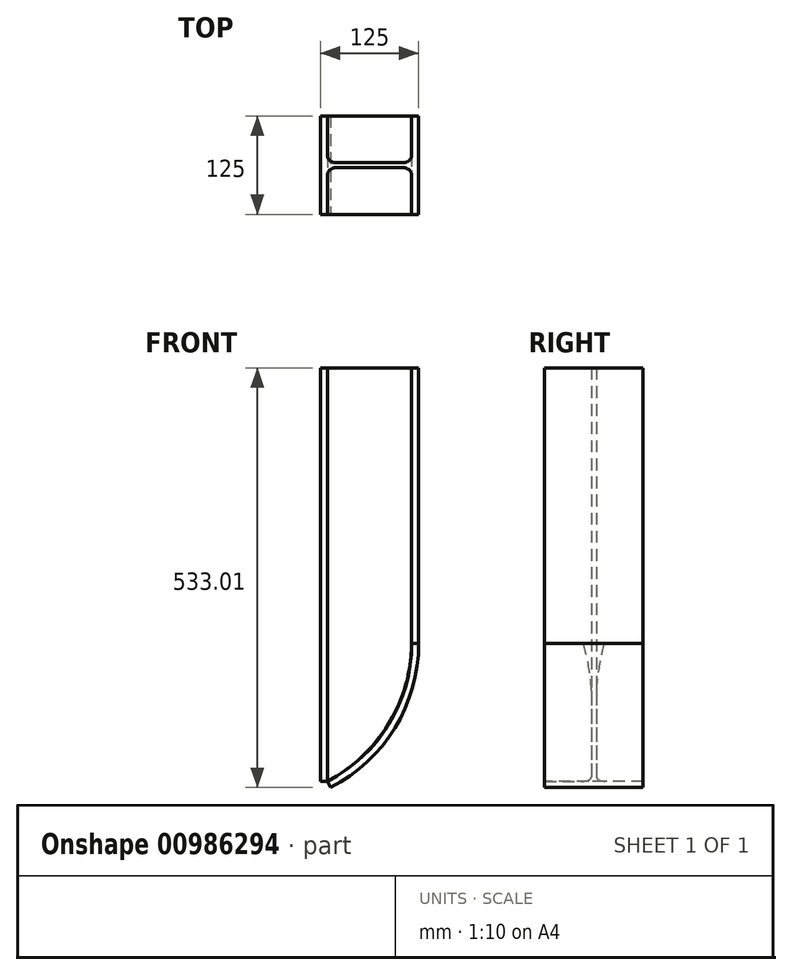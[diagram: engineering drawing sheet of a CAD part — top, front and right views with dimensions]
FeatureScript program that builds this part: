
annotation { "Feature Type Name" : "Feature", "Feature Type Description" : "" }
export const myFeature = defineFeature(function(context is Context, id is Id, definition is map)
    precondition{}
    {
        {
            var Q0;
            Q0=qCreatedBy(makeId("Top.planeOp"),FACE);
            var sketch = newSketch(context, id + "F0", { "sketchPlane" : qUnion([Q0])});
            skLineSegment(sketch, "E0.bottom", {"start": v(-62.5, 62.5) * mm, "end": v(62.5, 62.5) * mm});
            skLineSegment(sketch, "E0.top", {"start": v(-62.5, -62.5) * mm, "end": v(62.5, -62.5) * mm});
            skLineSegment(sketch, "E0.left", {"start": v(-62.5, 62.5) * mm, "end": v(-62.5, -62.5) * mm});
            skLineSegment(sketch, "E0.right", {"start": v(62.5, 62.5) * mm, "end": v(62.5, -62.5) * mm});
            skLineSegment(sketch, "E1.bottom", {"start": v(-53.5, 62.5) * mm, "end": v(53.5, 62.5) * mm});
            skLineSegment(sketch, "E1.top", {"start": v(-43.5, 3.25) * mm, "end": v(43.5, 3.25) * mm});
            skLineSegment(sketch, "E1.left", {"start": v(-53.5, 62.5) * mm, "end": v(-53.5, 13.25) * mm});
            skLineSegment(sketch, "E1.right", {"start": v(53.5, 62.5) * mm, "end": v(53.5, 13.25) * mm});
            skLineSegment(sketch, "E2.bottom", {"start": v(-53.5, -62.5) * mm, "end": v(53.5, -62.5) * mm});
            skLineSegment(sketch, "E2.top", {"start": v(-43.5, -3.25) * mm, "end": v(43.5, -3.25) * mm});
            skLineSegment(sketch, "E2.left", {"start": v(-53.5, -62.5) * mm, "end": v(-53.5, -13.25) * mm});
            skLineSegment(sketch, "E2.right", {"start": v(53.5, -62.5) * mm, "end": v(53.5, -13.25) * mm});
            skPoint(sketch, "E3.visualSharp", {"position": v(-53.5, 3.25) * mm});
            skArc(sketch, "E3.filletArc", {"start": v(-53.5, 13.25) * mm, "mid": v(-50.57, 6.18) * mm, "end": v(-43.5, 3.25) * mm});
            skPoint(sketch, "E4.visualSharp", {"position": v(53.5, 3.25) * mm});
            skArc(sketch, "E4.filletArc", {"start": v(43.5, 3.25) * mm, "mid": v(50.57, 6.18) * mm, "end": v(53.5, 13.25) * mm});
            skPoint(sketch, "E5.visualSharp", {"position": v(-53.5, -3.25) * mm});
            skArc(sketch, "E5.filletArc", {"start": v(-43.5, -3.25) * mm, "mid": v(-50.57, -6.18) * mm, "end": v(-53.5, -13.25) * mm});
            skPoint(sketch, "E6.visualSharp", {"position": v(53.5, -3.25) * mm});
            skArc(sketch, "E6.filletArc", {"start": v(53.5, -13.25) * mm, "mid": v(50.57, -6.18) * mm, "end": v(43.5, -3.25) * mm});
            skSolve(sketch);
        }
        {
            var Q0;
            {var subQ3=sQuery(id+"F0.wireOp",EDGE,"E0.left");Q0=makeQuery(id+"F0.imprint","IMPRINT",FACE,{"disambiguationData":[TD([[makeQuery(id+"F0.imprint","IMPRINT",EDGE,{"derivedFrom":subQ3}),1.0]])]});}
            extrude(context, id + "F1", {"entities" : qUnion([Q0]), "depth" : 525 * mm, "offsetDistance" : 25 * mm});
        }
        {
            var Q0;
            {var subQ0=sQuery(id+"F0.wireOp",EDGE,"E0.top");Q0=makeQuery(id+"F1.opExtrude","SWEPT_FACE",FACE,{"disambiguationData":[OSD([subQ0]),TDD([makeQuery(id+"F0.imprint","IMPRINT",EDGE,{"disambiguationData":[TD([[makeQuery(id+"F0.imprint","INTERSECT",VERTEX,{"derivedFrom":[subQ0,sQuery(id+"F0.wireOp",EDGE,"E0.left")]}),-1.0]])],"derivedFrom":subQ0})])]});}
            var sketch = newSketch(context, id + "F2", { "sketchPlane" : qUnion([Q0])});
            skLineSegment(sketch, "E7.bottom", {"start": v(-53.5, 0) * mm, "end": v(62.5, 0) * mm});
            skLineSegment(sketch, "E7.top", {"start": v(-53.5, 175) * mm, "end": v(62.5, 175) * mm});
            skLineSegment(sketch, "E7.left", {"start": v(-53.5, 0) * mm, "end": v(-53.5, 175) * mm});
            skLineSegment(sketch, "E7.right", {"start": v(62.5, 0) * mm, "end": v(62.5, 175) * mm});
            skArc(sketch, "E8", {"start": v(-53.5, 0) * mm, "mid": v(24.14, 72.74) * mm, "end": v(53.5, 175) * mm});
            skSolve(sketch);
        }
        {
            var Q0;
            Q0=makeQuery(id+"F2.imprint","IMPRINT",FACE,{"disambiguationData":[TD([[makeQuery(id+"F2.imprint","IMPRINT",EDGE,{"derivedFrom":sQuery(id+"F2.wireOp",EDGE,"E7.bottom")}),1.0]])]});
            extrude(context, id + "F3", {"entities" : qUnion([Q0]), "operationType" : NewBodyOperationType.REMOVE, "oppositeDirection" : true, "depth" : 125 * mm, "offsetDistance" : 25 * mm});
        }
        {
            var Q0;
            {var subQ0=sQuery(id+"F0.wireOp",EDGE,"E0.top");Q0=makeQuery(id+"F1.opExtrude","SWEPT_FACE",FACE,{"disambiguationData":[OSD([subQ0]),TDD([makeQuery(id+"F0.imprint","IMPRINT",EDGE,{"disambiguationData":[TD([[makeQuery(id+"F0.imprint","INTERSECT",VERTEX,{"derivedFrom":[subQ0,sQuery(id+"F0.wireOp",EDGE,"E0.right")]}),1.0]])],"derivedFrom":subQ0})])]});}
            var sketch = newSketch(context, id + "F4", { "sketchPlane" : qUnion([Q0])});
            skArc(sketch, "E9", {"start": v(-53.45, 0) * mm, "mid": v(24.65, 72.45) * mm, "end": v(53.5, 175) * mm});
            skArc(sketch, "E10.0", {"start": v(-49.34, -8) * mm, "mid": v(32.33, 67.76) * mm, "end": v(62.5, 175) * mm});
            skLineSegment(sketch, "E11", {"start": v(53.5, 175) * mm, "end": v(62.5, 175) * mm});
            skLineSegment(sketch, "E12", {"start": v(-53.45, 0) * mm, "end": v(-49.34, -8) * mm});
            skSolve(sketch);
        }
        {
            var Q0;
            Q0=makeQuery(id+"F4.imprint","IMPRINT",FACE,{"disambiguationData":[TD([[makeQuery(id+"F4.imprint","IMPRINT",EDGE,{"derivedFrom":sQuery(id+"F4.wireOp",EDGE,"E9")}),-1.0]])]});
            extrude(context, id + "F5", {"entities" : qUnion([Q0]), "oppositeDirection" : true, "depth" : 125 * mm, "offsetDistance" : 25 * mm});
        }
    });
